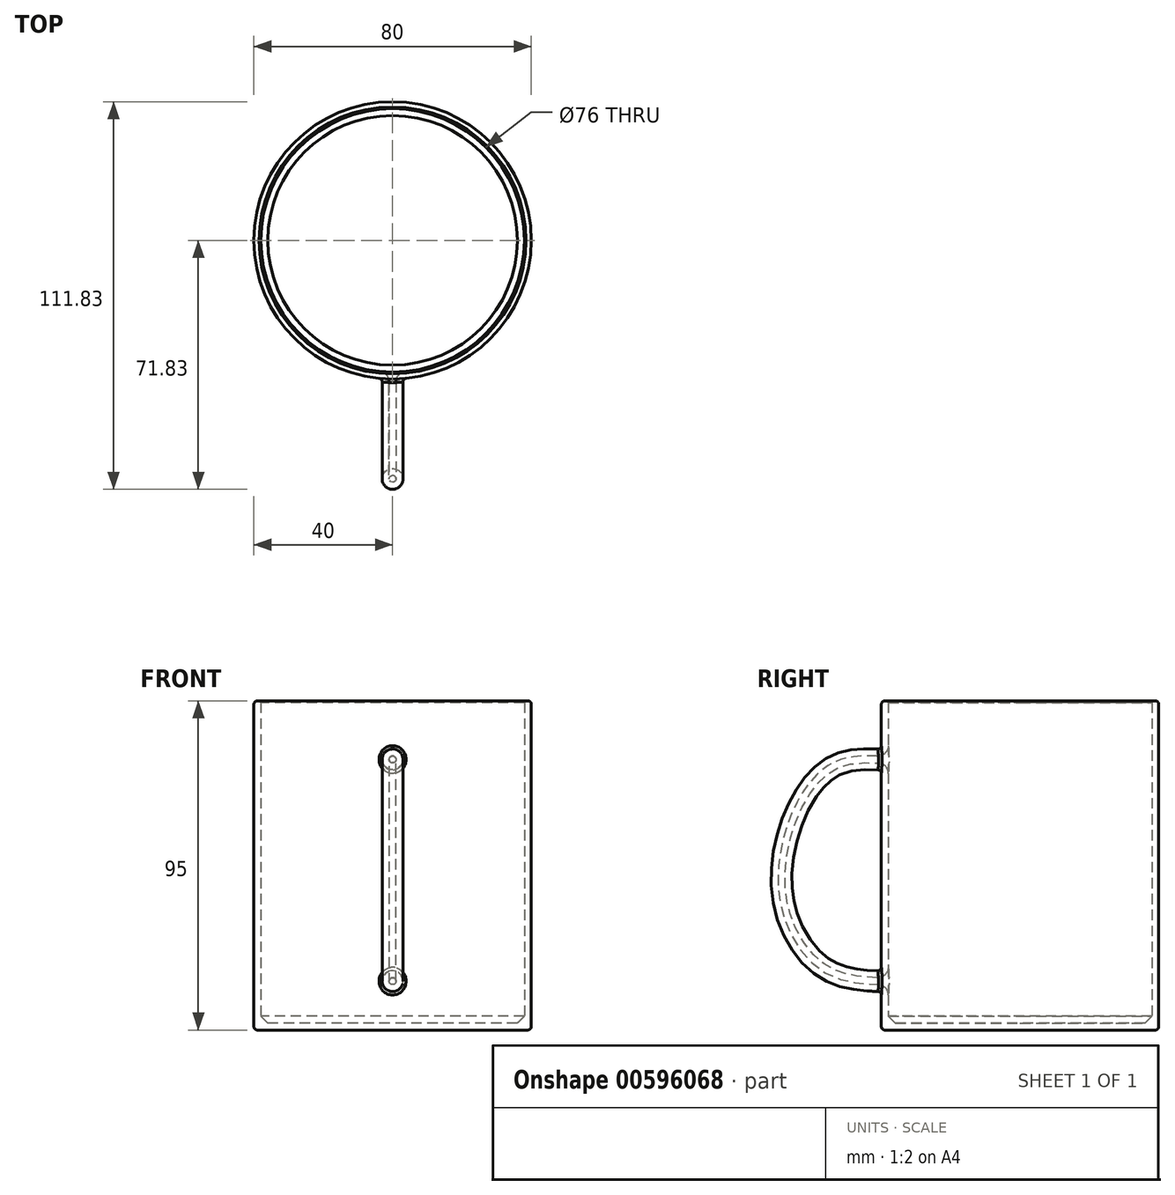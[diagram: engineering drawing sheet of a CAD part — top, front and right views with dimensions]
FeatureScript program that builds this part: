
annotation { "Feature Type Name" : "Feature", "Feature Type Description" : "" }
export const myFeature = defineFeature(function(context is Context, id is Id, definition is map)
    precondition{}
    {
        {
            var Q0;
            Q0=qCreatedBy(makeId("Top.planeOp"),FACE);
            var sketch = newSketch(context, id + "F0", { "sketchPlane" : qUnion([Q0])});
            skCircle(sketch, "E0", {"center": v(0, 0) * mm, "radius": 40 * mm});
            skSolve(sketch);
        }
        {
            var Q0;
            Q0 = qSketchRegion(id + "F0", true);
            extrude(context, id + "F1", {"entities" : qUnion([Q0]), "depth" : 95 * mm, "offsetDistance" : 25 * mm});
        }
        {
            var Q0;
            Q0=qCreatedBy(makeId("Front.planeOp"),FACE);
            cPlane(context, id + "F2", {"entities" : qUnion([Q0]), "cplaneType" : CPlaneType.OFFSET, "offset" : 40 * mm, "width" : 150 * mm, "height" : 150 * mm});
        }
        {
            var Q0;
            Q0=qCreatedBy(makeId("Right.planeOp"),FACE);
            var sketch = newSketch(context, id + "F3", { "sketchPlane" : qUnion([Q0])});
            skFitSpline(sketch, "E1", {"points": [v(-39.54, 13.87) * mm, v(-56.1, 17.41) * mm, v(-68.28, 36.38) * mm, v(-64.88, 62.7) * mm, v(-53.27, 76.58) * mm, v(-39.12, 78.14) * mm], "startDerivative": vector(-92.89, 3.76) * mm, "endDerivative": vector(86.6, -4.08) * mm});
            skSolve(sketch);
        }
        {
            var Q0;
            Q0=qCreatedBy(id+"F2.planeOp",FACE);
            var sketch = newSketch(context, id + "F4", { "sketchPlane" : qUnion([Q0])});
            skCircle(sketch, "E2", {"center": v(0, 14.06) * mm, "radius": 3 * mm});
            skSolve(sketch);
        }
        {
            var Q0;
            Q0 = qSketchRegion(id + "F4", true);
            var Q1;
            Q1 = qConstructionFilter(qBodyType(qCreatedBy(id + "F3" ,EDGE), BodyType.WIRE), ConstructionObject.NO);
            sweep(context, id + "F5", {"operationType" : NewBodyOperationType.ADD, "profiles" : qUnion([Q0]), "path" : qUnion([Q1])});
        }
        {
            var Q0;
            Q0=makeQuery(id+"F1.opExtrude","CAP_FACE",FACE,{"disambiguationData":[OSD([sQuery(id+"F0.wireOp",EDGE,"E0")])],"isStart":false});
            shell(context, id + "F6", {"entities" : qUnion([Q0]), "thickness" : 2 * mm});
        }
        {
            var Q0;
            Q0=makeQuery(id+"F1.opExtrude","CAP_EDGE",EDGE,{"disambiguationData":[OSD([sQuery(id+"F0.wireOp",EDGE,"E0")])],"isStart":false});
            fillet(context, id + "F7", {"entities" : qUnion([Q0]), "radius" : 1 * mm, "tangentPropagation" : true, "allowEdgeOverflow" : false});
        }
        {
            var Q0;
            {var subQ0=sQuery(id+"F0.wireOp",EDGE,"E0");Q0=makeQuery(id+"F6.opShell","OFFSET_EDGE",EDGE,{"disambiguationData":[OSD([subQ0]),TDD([makeQuery(id+"F1.opExtrude","CAP_EDGE",EDGE,{"disambiguationData":[OSD([subQ0])],"isStart":false})])]});}
            chamfer(context, id + "F8", {"entities" : qUnion([Q0]), "width" : .5 * mm, "tangentPropagation" : true});
        }
        {
            var Q0;
            Q0=makeQuery(id+"F5.boolean.opBoolean","INTERSECT",EDGE,{"disambiguationData":[OD(1.0)],"derivedFrom":[makeQuery(id+"F1.opExtrude","SWEPT_FACE",FACE,{"disambiguationData":[OSD([sQuery(id+"F0.wireOp",EDGE,"E0")])]}),makeQuery(id+"F5.opSweep","SWEPT_FACE",FACE,{"disambiguationData":[OSD([sQuery(id+"F3.wireOp",EDGE,"E1"),sQuery(id+"F4.wireOp",EDGE,"E2")])]})]});
            var Q1;
            Q1=makeQuery(id+"F5.boolean.opBoolean","INTERSECT",EDGE,{"disambiguationData":[OD(0.0)],"derivedFrom":[makeQuery(id+"F1.opExtrude","SWEPT_FACE",FACE,{"disambiguationData":[OSD([sQuery(id+"F0.wireOp",EDGE,"E0")])]}),makeQuery(id+"F5.opSweep","SWEPT_FACE",FACE,{"disambiguationData":[OSD([sQuery(id+"F3.wireOp",EDGE,"E1"),sQuery(id+"F4.wireOp",EDGE,"E2")])]})]});
            fillet(context, id + "F9", {"entities" : qUnion([Q0, Q1]), "radius" : 1 * mm, "tangentPropagation" : true, "allowEdgeOverflow" : false});
        }
        {
            var Q0;
            Q0=makeQuery(id+"F1.opExtrude","CAP_EDGE",EDGE,{"disambiguationData":[OSD([sQuery(id+"F0.wireOp",EDGE,"E0")])],"isStart":true});
            fillet(context, id + "F10", {"entities" : qUnion([Q0]), "radius" : 1 * mm, "tangentPropagation" : true, "allowEdgeOverflow" : false});
        }
        {
            var Q0;
            {var subQ0=sQuery(id+"F0.wireOp",EDGE,"E0");Q0=makeQuery(id+"F6.opShell","OFFSET_EDGE",EDGE,{"disambiguationData":[OSD([subQ0]),TDD([makeQuery(id+"F1.opExtrude","CAP_EDGE",EDGE,{"disambiguationData":[OSD([subQ0])],"isStart":true})])]});}
            chamfer(context, id + "F11", {"entities" : qUnion([Q0]), "width" : 2 * mm, "tangentPropagation" : true});
        }
        {
            var Q0;
            {var subQ0=sQuery(id+"F4.wireOp",EDGE,"E2");var subQ1=sQuery(id+"F3.wireOp",EDGE,"E1");var subQ2=sQuery(id+"F0.wireOp",EDGE,"E0");Q0=makeQuery(id+"F6.opShell","OFFSET_EDGE",EDGE,{"disambiguationData":[OSD([subQ2,subQ1,subQ0]),TDD([makeQuery(id+"F5.boolean.opBoolean","INTERSECT",EDGE,{"disambiguationData":[OD(0.0)],"derivedFrom":[makeQuery(id+"F1.opExtrude","SWEPT_FACE",FACE,{"disambiguationData":[OSD([subQ2])]}),makeQuery(id+"F5.opSweep","SWEPT_FACE",FACE,{"disambiguationData":[OSD([subQ1,subQ0])]})]})])]});}
            var Q1;
            {var subQ0=sQuery(id+"F4.wireOp",EDGE,"E2");var subQ1=sQuery(id+"F3.wireOp",EDGE,"E1");var subQ2=sQuery(id+"F0.wireOp",EDGE,"E0");Q1=makeQuery(id+"F6.opShell","OFFSET_EDGE",EDGE,{"disambiguationData":[OSD([subQ2,subQ1,subQ0]),TDD([makeQuery(id+"F5.boolean.opBoolean","INTERSECT",EDGE,{"disambiguationData":[OD(1.0)],"derivedFrom":[makeQuery(id+"F1.opExtrude","SWEPT_FACE",FACE,{"disambiguationData":[OSD([subQ2])]}),makeQuery(id+"F5.opSweep","SWEPT_FACE",FACE,{"disambiguationData":[OSD([subQ1,subQ0])]})]})])]});}
            fillet(context, id + "F12", {"entities" : qUnion([Q0, Q1]), "radius" : 3 * mm, "tangentPropagation" : true, "allowEdgeOverflow" : false});
        }
    });
